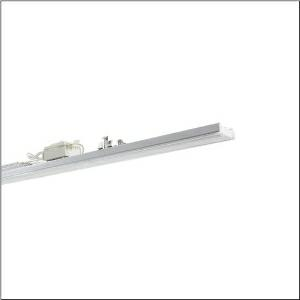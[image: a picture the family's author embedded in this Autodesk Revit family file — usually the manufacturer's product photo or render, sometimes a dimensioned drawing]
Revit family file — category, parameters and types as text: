
# Revit family: licross_r__11_recessed_ho_51tl1wcn4c5m_93f9
name_source: partatom
category: Lighting Fixtures
units: mm (PartAtom-declared; Revit-internal decimal feet)

## family parameters
Cut with Voids When Loaded = No
Host = Face
Light Source = No
Part Type = Normal
Room Calculation Point = No
Round Connector Dimension = Use Diameter
Shared = No

## types (1)
- --- (1 x LED, 12870 lm, 66.5 W, 4000K)
    Apparent Load = 67 VA
    CIE Flux Codes = 73 94 99 100 100
    Color Rendering = 80
    Color Temperature = 4000K
    Default Elevation = 1800 mm
    Description = Licross® 11 Recessed HO, luminaire insert, of sheet steel, coil coated, white, length: 1.500mm, width: 66mm, height: 67mm, LED rated luminous flux: 12.870lm, light colour: 840, control gear: ON/OFF Multilumen, CLOi, with plug, 3-pole, with phase selection, mains connection: 220..240V, AC, 50/60Hz, start of lifetime: 67W, end of service life: 75W, internal wiring halogen-free, primary optical cover: cover, of PMMA, light emission: direct distribution, primary light characteristic: symmetric, protection rating (complete): IP40, insulation class (complete): insulation class I (protective earthing), certification: CE, ENEC, VDE, UKCA, protection symbol: D if used in an environment without relevant dust loads with corresponding accessories, impact resistance: IK06, permissible ambient temperature for indoor applications: -35..+35°C, corresponds to IFS (International Featured Standards) requirements for safety and quality in the food industry, reducing of maximum allowable ambient temperature of 5°C with ceiling mounting, LABS conformity tested according to VDMA 24364:2018-05, packaging unit: 1 piece
    Height = 58 mm
    Lamp = 1 x LED
    Lamp Light Flux = 12870 lm
    Lamp Power = 66.5 W
    Lamp count = 1
    Length = 1500 mm
    Luminous efficacy = 194 lm/W
    Manufacturer = Siteco
    ModVariant = No
    Model = 51TL1WCN4C5M
    Mounting Place = Ceiling
    Mounting Type = Pendant
    Number of Poles = 1
    OnlyDefault = Yes
    Power Factor = 1
    Product Name = Licross® 11 Recessed HO
    Product group = luminaire insert | ceiling pendant
    ProductGroupID = 902
    Protection Class = Protection class I
    Protection Degree = IP 40
    RLX_Detail_Level = 1
    RLX_Emergency_Light_Flux = 0 lm
    RLX_Emergency_Type = 0
    RLX_Emergency_Type_DB = No
    RlxData = <blob elided: 22353 chars, md5=07480b27>
    Socket = socket
    Standby Power = 0 W
    System Light Flux = 12870 lm
    System Power = 67 W
    Type Comments = factory setting: luminous flux: 100 % | (A | C | E) | 156 mA
    Type Image = l_1296930.jpg
    URL = http://relux.com
    VarID = @adj_080133
    Voltage = 0 V
    Weight = 0.00 kg
    Width = 66 mm

## geometry (parser evidence)
native form markers: Blend x4, Sweep x9
no freeform markers — native parametric forms only
